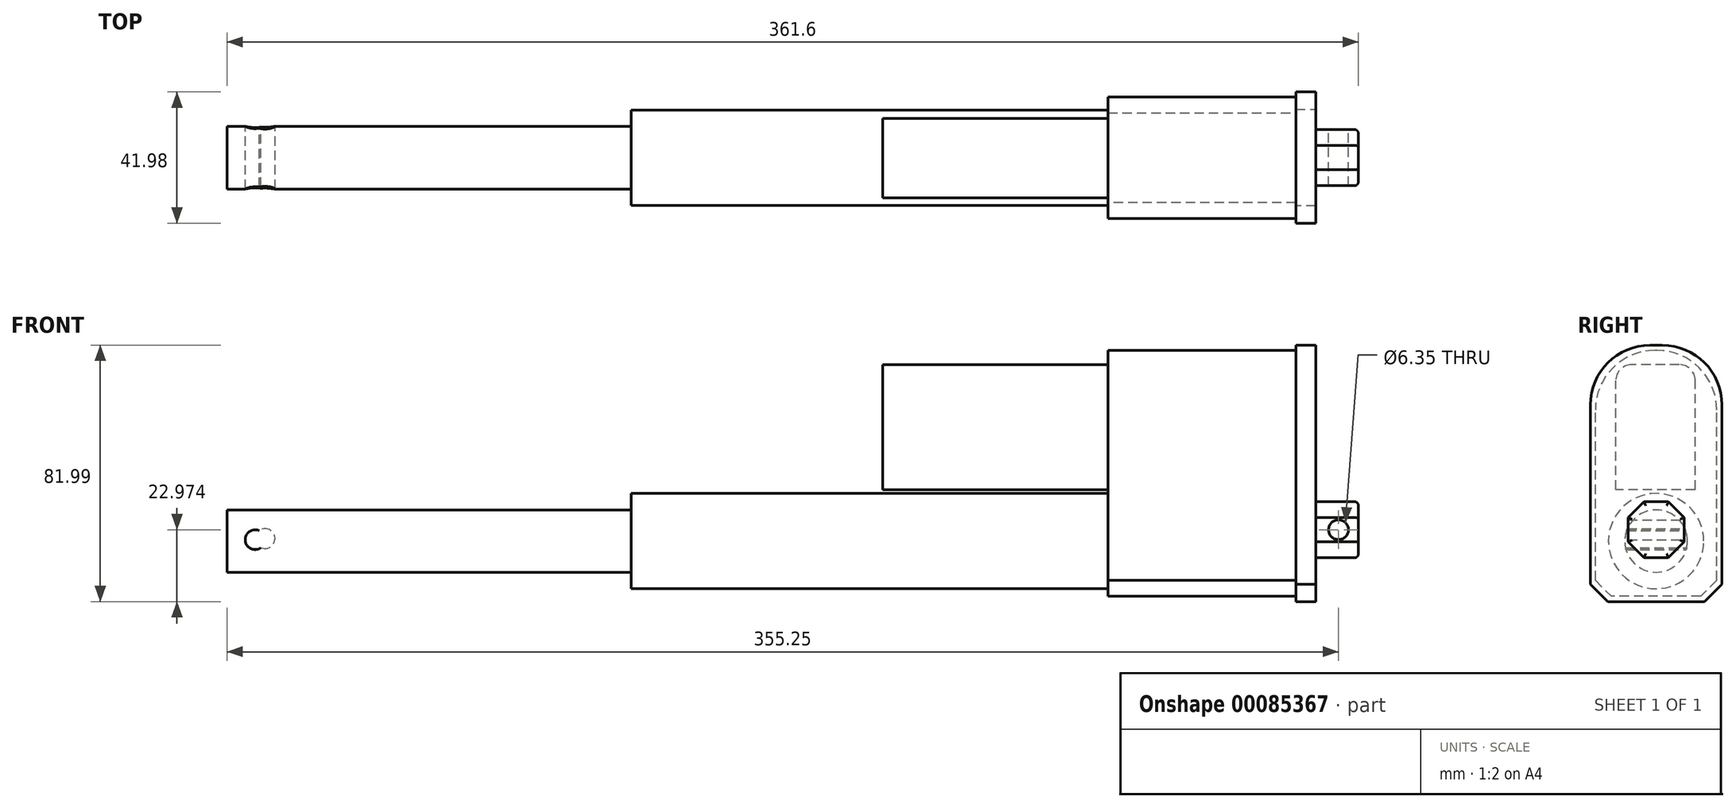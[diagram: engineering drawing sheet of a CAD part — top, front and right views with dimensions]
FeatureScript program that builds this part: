
annotation { "Feature Type Name" : "Feature", "Feature Type Description" : "" }
export const myFeature = defineFeature(function(context is Context, id is Id, definition is map)
    precondition{}
    {
        {
            var Q0;
            Q0=qCreatedBy(makeId("Right.planeOp"),FACE);
            var sketch = newSketch(context, id + "F0", { "sketchPlane" : qUnion([Q0])});
            skLineSegment(sketch, "E0.bottom", {"start": v(-11.88, 50.5) * mm, "end": v(-8, 50.5) * mm});
            skLineSegment(sketch, "E0.top", {"start": v(-30.93, -31.5) * mm, "end": v(11.05, -31.5) * mm});
            skLineSegment(sketch, "E0.left", {"start": v(-30.93, 31.44) * mm, "end": v(-30.93, -31.5) * mm});
            skLineSegment(sketch, "E0.right", {"start": v(11.05, 31.44) * mm, "end": v(11.05, -31.5) * mm});
            skLineSegment(sketch, "E1.bottom", {"start": v(-18.93, 0.47) * mm, "end": v(-0.95, 0.47) * mm});
            skLineSegment(sketch, "E1.top", {"start": v(-18.93, -17.52) * mm, "end": v(-0.95, -17.52) * mm});
            skLineSegment(sketch, "E1.left", {"start": v(-18.93, 0.47) * mm, "end": v(-18.93, -17.52) * mm});
            skLineSegment(sketch, "E1.right", {"start": v(-0.95, 0.47) * mm, "end": v(-0.95, -17.52) * mm});
            skPoint(sketch, "E2.visualSharp", {"position": v(-30.93, 50.5) * mm});
            skArc(sketch, "E2.filletArc", {"start": v(-11.88, 50.5) * mm, "mid": v(-25.35, 44.91) * mm, "end": v(-30.93, 31.44) * mm});
            skPoint(sketch, "E3.visualSharp", {"position": v(11.05, 50.5) * mm});
            skArc(sketch, "E3.filletArc", {"start": v(11.05, 31.44) * mm, "mid": v(5.47, 44.91) * mm, "end": v(-8, 50.5) * mm});
            skSolve(sketch);
        }
        {
            var Q0;
            Q0=makeQuery(id+"F0.imprint","IMPRINT",FACE,{"disambiguationData":[TD([[makeQuery(id+"F0.imprint","IMPRINT",EDGE,{"derivedFrom":sQuery(id+"F0.wireOp",EDGE,"E1.bottom")}),-1.0]])]});
            extrude(context, id + "F1", {"entities" : qUnion([Q0]), "depth" : 19.99 * mm});
        }
        {
            var Q0;
            Q0=qSketchRegion(id+"F0",true);
            extrude(context, id + "F2", {"entities" : qUnion([Q0]), "operationType" : NewBodyOperationType.ADD, "depth" : 6.35 * mm});
        }
        {
            var Q0;
            Q0=makeQuery(id+"F1.opExtrude","SWEPT_EDGE",EDGE,{"disambiguationData":[OSD([sQuery(id+"F0.wireOp",EDGE,"E1.bottom"),sQuery(id+"F0.wireOp",EDGE,"E1.left")])]});
            var Q1;
            Q1=makeQuery(id+"F1.opExtrude","SWEPT_EDGE",EDGE,{"disambiguationData":[OSD([sQuery(id+"F0.wireOp",EDGE,"E1.top"),sQuery(id+"F0.wireOp",EDGE,"E1.left")])]});
            var Q2;
            Q2=makeQuery(id+"F1.opExtrude","SWEPT_EDGE",EDGE,{"disambiguationData":[OSD([sQuery(id+"F0.wireOp",EDGE,"E1.top"),sQuery(id+"F0.wireOp",EDGE,"E1.right")])]});
            var Q3;
            Q3=makeQuery(id+"F1.opExtrude","SWEPT_EDGE",EDGE,{"disambiguationData":[OSD([sQuery(id+"F0.wireOp",EDGE,"E1.bottom"),sQuery(id+"F0.wireOp",EDGE,"E1.right")])]});
            chamfer(context, id + "F3", {"entities" : qUnion([Q0, Q1, Q2, Q3]), "width" : 5.08 * mm, "tangentPropagation" : true});
        }
        {
            var Q0;
            Q0=makeQuery(id+"F1.opExtrude","SWEPT_FACE",FACE,{"disambiguationData":[OSD([sQuery(id+"F0.wireOp",EDGE,"E1.right")])]});
            var sketch = newSketch(context, id + "F4", { "sketchPlane" : qUnion([Q0])});
            skCircle(sketch, "E4", {"center": v(-13.64, -8.53) * mm, "radius": 3.18 * mm});
            skSolve(sketch);
        }
        {
            var Q0;
            Q0=makeQuery(id+"F4.imprint","IMPRINT",FACE,{"disambiguationData":[TD([[makeQuery(id+"F4.imprint","IMPRINT",EDGE,{"derivedFrom":sQuery(id+"F4.wireOp",EDGE,"E4")}),1.0]])]});
            extrude(context, id + "F5", {"entities" : qUnion([Q0]), "operationType" : NewBodyOperationType.REMOVE, "endBound" : BoundingType.THROUGH_ALL, "oppositeDirection" : true, "depth" : 25.4 * mm});
        }
        {
            var Q0;
            Q0=makeQuery(id+"F1.opExtrude","CAP_FACE",FACE,{"disambiguationData":[OSD([sQuery(id+"F0.wireOp",EDGE,"E1.bottom"),sQuery(id+"F0.wireOp",EDGE,"E1.top"),sQuery(id+"F0.wireOp",EDGE,"E1.left"),sQuery(id+"F0.wireOp",EDGE,"E1.right")])],"isStart":false});
            fillet(context, id + "F6", {"entities" : qUnion([Q0]), "radius" : 1.27 * mm, "tangentPropagation" : true, "allowEdgeOverflow" : false});
        }
        {
            var Q0;
            {var subQ0=sQuery(id+"F0.wireOp",EDGE,"E1.bottom");var subQ1=sQuery(id+"F0.wireOp",EDGE,"E1.top");var subQ2=sQuery(id+"F0.wireOp",EDGE,"E1.left");var subQ3=sQuery(id+"F0.wireOp",EDGE,"E1.right");Q0=makeQuery(id+"F2.boolean.opBoolean","MERGE",FACE,{"derivedFrom":[makeQuery(id+"F1.opExtrude","CAP_FACE",FACE,{"disambiguationData":[OSD([subQ0,subQ1,subQ2,subQ3])],"isStart":true}),makeQuery(id+"F2.opExtrude","CAP_FACE",FACE,{"disambiguationData":[OSD([sQuery(id+"F0.wireOp",EDGE,"E0.top"),sQuery(id+"F0.wireOp",EDGE,"E0.left"),sQuery(id+"F0.wireOp",EDGE,"E0.right"),subQ0,subQ1,subQ2,subQ3,sQuery(id+"F0.wireOp",EDGE,"E2.filletArc"),sQuery(id+"F0.wireOp",EDGE,"E3.filletArc"),sQuery(id+"F0.wireOp",EDGE,"E0.bottom")])],"isStart":true})]});}
            var sketch = newSketch(context, id + "F7", { "sketchPlane" : qUnion([Q0])});
            skLineSegment(sketch, "E5.bottom", {"start": v(-9.42, -29.78) * mm, "end": v(29.37, -29.78) * mm});
            skLineSegment(sketch, "E5.top", {"start": v(9.63, 48.83) * mm, "end": v(10.32, 48.83) * mm});
            skLineSegment(sketch, "E5.left", {"start": v(-9.42, -29.78) * mm, "end": v(-9.42, 29.78) * mm});
            skLineSegment(sketch, "E5.right", {"start": v(29.37, -29.78) * mm, "end": v(29.37, 29.78) * mm});
            skPoint(sketch, "E6.visualSharp", {"position": v(-9.42, 48.83) * mm});
            skArc(sketch, "E6.filletArc", {"start": v(9.63, 48.83) * mm, "mid": v(-3.84, 43.25) * mm, "end": v(-9.42, 29.78) * mm});
            skPoint(sketch, "E7.visualSharp", {"position": v(29.37, 48.83) * mm});
            skArc(sketch, "E7.filletArc", {"start": v(29.37, 29.78) * mm, "mid": v(23.79, 43.25) * mm, "end": v(10.32, 48.83) * mm});
            skSolve(sketch);
        }
        {
            var Q0;
            Q0=makeQuery(id+"F7.imprint","IMPRINT",FACE,{"disambiguationData":[TD([[makeQuery(id+"F7.imprint","IMPRINT",EDGE,{"derivedFrom":sQuery(id+"F7.wireOp",EDGE,"E5.bottom")}),1.0]])]});
            extrude(context, id + "F8", {"entities" : qUnion([Q0]), "operationType" : NewBodyOperationType.ADD, "depth" : 60 * mm});
        }
        {
            var Q0;
            Q0=makeQuery(id+"F8.opExtrude","SWEPT_EDGE",EDGE,{"disambiguationData":[OSD([sQuery(id+"F7.wireOp",EDGE,"E5.bottom"),sQuery(id+"F7.wireOp",EDGE,"E5.left")])]});
            var Q1;
            Q1=makeQuery(id+"F8.opExtrude","SWEPT_EDGE",EDGE,{"disambiguationData":[OSD([sQuery(id+"F7.wireOp",EDGE,"E5.bottom"),sQuery(id+"F7.wireOp",EDGE,"E5.right")])]});
            chamfer(context, id + "F9", {"entities" : qUnion([Q0, Q1]), "width" : 5.08 * mm, "tangentPropagation" : true});
        }
        {
            var Q0;
            Q0=makeQuery(id+"F2.opExtrude","SWEPT_EDGE",EDGE,{"disambiguationData":[OSD([sQuery(id+"F0.wireOp",EDGE,"E0.top"),sQuery(id+"F0.wireOp",EDGE,"E0.left")])]});
            var Q1;
            Q1=makeQuery(id+"F2.opExtrude","SWEPT_EDGE",EDGE,{"disambiguationData":[OSD([sQuery(id+"F0.wireOp",EDGE,"E0.top"),sQuery(id+"F0.wireOp",EDGE,"E0.right")])]});
            chamfer(context, id + "F10", {"entities" : qUnion([Q0, Q1]), "width" : 5.6 * mm});
        }
        {
            var Q0;
            Q0=makeQuery(id+"F8.opExtrude","CAP_FACE",FACE,{"disambiguationData":[OSD([sQuery(id+"F7.wireOp",EDGE,"E5.bottom"),sQuery(id+"F7.wireOp",EDGE,"E5.top"),sQuery(id+"F7.wireOp",EDGE,"E5.left"),sQuery(id+"F7.wireOp",EDGE,"E5.right"),sQuery(id+"F7.wireOp",EDGE,"E6.filletArc"),sQuery(id+"F7.wireOp",EDGE,"E7.filletArc")])],"isStart":false});
            var sketch = newSketch(context, id + "F11", { "sketchPlane" : qUnion([Q0])});
            skLineSegment(sketch, "E8.bottom", {"start": v(-2.56, 4.3) * mm, "end": v(22.84, 4.3) * mm});
            skLineSegment(sketch, "E8.top", {"start": v(2.52, 44.28) * mm, "end": v(17.76, 44.28) * mm});
            skLineSegment(sketch, "E8.left", {"start": v(-2.56, 4.3) * mm, "end": v(-2.56, 39.2) * mm});
            skLineSegment(sketch, "E8.right", {"start": v(22.84, 4.3) * mm, "end": v(22.84, 39.2) * mm});
            skPoint(sketch, "E9.visualSharp", {"position": v(-2.56, 44.28) * mm});
            skArc(sketch, "E9.filletArc", {"start": v(2.52, 44.28) * mm, "mid": v(-1.08, 42.8) * mm, "end": v(-2.56, 39.2) * mm});
            skPoint(sketch, "E10.visualSharp", {"position": v(22.84, 44.28) * mm});
            skArc(sketch, "E10.filletArc", {"start": v(22.84, 39.2) * mm, "mid": v(21.35, 42.8) * mm, "end": v(17.76, 44.28) * mm});
            skSolve(sketch);
        }
        {
            var Q0;
            Q0=makeQuery(id+"F11.imprint","IMPRINT",FACE,{"disambiguationData":[TD([[makeQuery(id+"F11.imprint","IMPRINT",EDGE,{"derivedFrom":sQuery(id+"F11.wireOp",EDGE,"E8.bottom")}),1.0]])]});
            extrude(context, id + "F12", {"entities" : qUnion([Q0]), "operationType" : NewBodyOperationType.ADD, "depth" : 71.98 * mm});
        }
        {
            var Q0;
            Q0=makeQuery(id+"F8.opExtrude","CAP_FACE",FACE,{"disambiguationData":[OSD([sQuery(id+"F7.wireOp",EDGE,"E5.bottom"),sQuery(id+"F7.wireOp",EDGE,"E5.top"),sQuery(id+"F7.wireOp",EDGE,"E5.left"),sQuery(id+"F7.wireOp",EDGE,"E5.right"),sQuery(id+"F7.wireOp",EDGE,"E6.filletArc"),sQuery(id+"F7.wireOp",EDGE,"E7.filletArc")])],"isStart":false});
            var sketch = newSketch(context, id + "F13", { "sketchPlane" : qUnion([Q0])});
            skCircle(sketch, "E11", {"center": v(9.98, -12.16) * mm, "radius": 15.24 * mm});
            skSolve(sketch);
        }
        {
            var Q0;
            Q0=makeQuery(id+"F13.imprint","IMPRINT",FACE,{"disambiguationData":[TD([[makeQuery(id+"F13.imprint","IMPRINT",EDGE,{"derivedFrom":sQuery(id+"F13.wireOp",EDGE,"E11")}),1.0]])]});
            extrude(context, id + "F14", {"entities" : qUnion([Q0]), "operationType" : NewBodyOperationType.ADD, "depth" : 152.4 * mm});
        }
        {
            var Q0;
            Q0=makeQuery(id+"F14.opExtrude","CAP_FACE",FACE,{"disambiguationData":[OSD([sQuery(id+"F13.wireOp",EDGE,"E11")])],"isStart":false});
            var sketch = newSketch(context, id + "F15", { "sketchPlane" : qUnion([Q0])});
            skCircle(sketch, "E12", {"center": v(9.98, -12.16) * mm, "radius": 10 * mm});
            skSolve(sketch);
        }
        {
            var Q0;
            Q0=makeQuery(id+"F15.imprint","IMPRINT",FACE,{"disambiguationData":[TD([[makeQuery(id+"F15.imprint","IMPRINT",EDGE,{"derivedFrom":sQuery(id+"F15.wireOp",EDGE,"E12")}),1.0]])]});
            extrude(context, id + "F16", {"entities" : qUnion([Q0]), "depth" : 129.22 * mm});
        }
        {
            var Q0;
            Q0=makeQuery(id+"F8.opExtrude","SWEPT_FACE",FACE,{"disambiguationData":[OSD([sQuery(id+"F7.wireOp",EDGE,"E5.left")])]});
            var sketch = newSketch(context, id + "F17", { "sketchPlane" : qUnion([Q0])});
            skCircle(sketch, "E13", {"center": v(329.44, -11.35) * mm, "radius": 3.18 * mm});
            skSolve(sketch);
        }
        {
            var Q0;
            Q0=makeQuery(id+"F17.imprint","IMPRINT",FACE,{"disambiguationData":[TD([[makeQuery(id+"F17.imprint","IMPRINT",EDGE,{"derivedFrom":sQuery(id+"F17.wireOp",EDGE,"E13")}),1.0]])]});
            extrude(context, id + "F18", {"entities" : qUnion([Q0]), "operationType" : NewBodyOperationType.REMOVE, "endBound" : BoundingType.THROUGH_ALL, "oppositeDirection" : true, "depth" : 25.4 * mm});
        }
        {
            var Q0;
            Q0=qCreatedBy(makeId("Front.planeOp"),FACE);
            var sketch = newSketch(context, id + "F19", { "sketchPlane" : qUnion([Q0])});
            skCircle(sketch, "E14", {"center": v(-332.62, -11.7) * mm, "radius": 3.18 * mm});
            skSolve(sketch);
        }
        {
            var Q0;
            Q0=makeQuery(id+"F19.imprint","IMPRINT",FACE,{"disambiguationData":[TD([[makeQuery(id+"F19.imprint","IMPRINT",EDGE,{"derivedFrom":sQuery(id+"F19.wireOp",EDGE,"E14")}),1.0]])]});
            extrude(context, id + "F20", {"entities" : qUnion([Q0]), "operationType" : NewBodyOperationType.REMOVE, "endBound" : BoundingType.THROUGH_ALL, "depth" : 25.4 * mm});
        }
        {
            var Q0;
            Q0=makeQuery(id+"F19.imprint","IMPRINT",FACE,{"disambiguationData":[TD([[makeQuery(id+"F19.imprint","IMPRINT",EDGE,{"derivedFrom":sQuery(id+"F19.wireOp",EDGE,"E14")}),1.0]])]});
            extrude(context, id + "F21", {"entities" : qUnion([Q0]), "operationType" : NewBodyOperationType.REMOVE, "endBound" : BoundingType.THROUGH_ALL, "oppositeDirection" : true, "depth" : 25.4 * mm});
        }
    });
